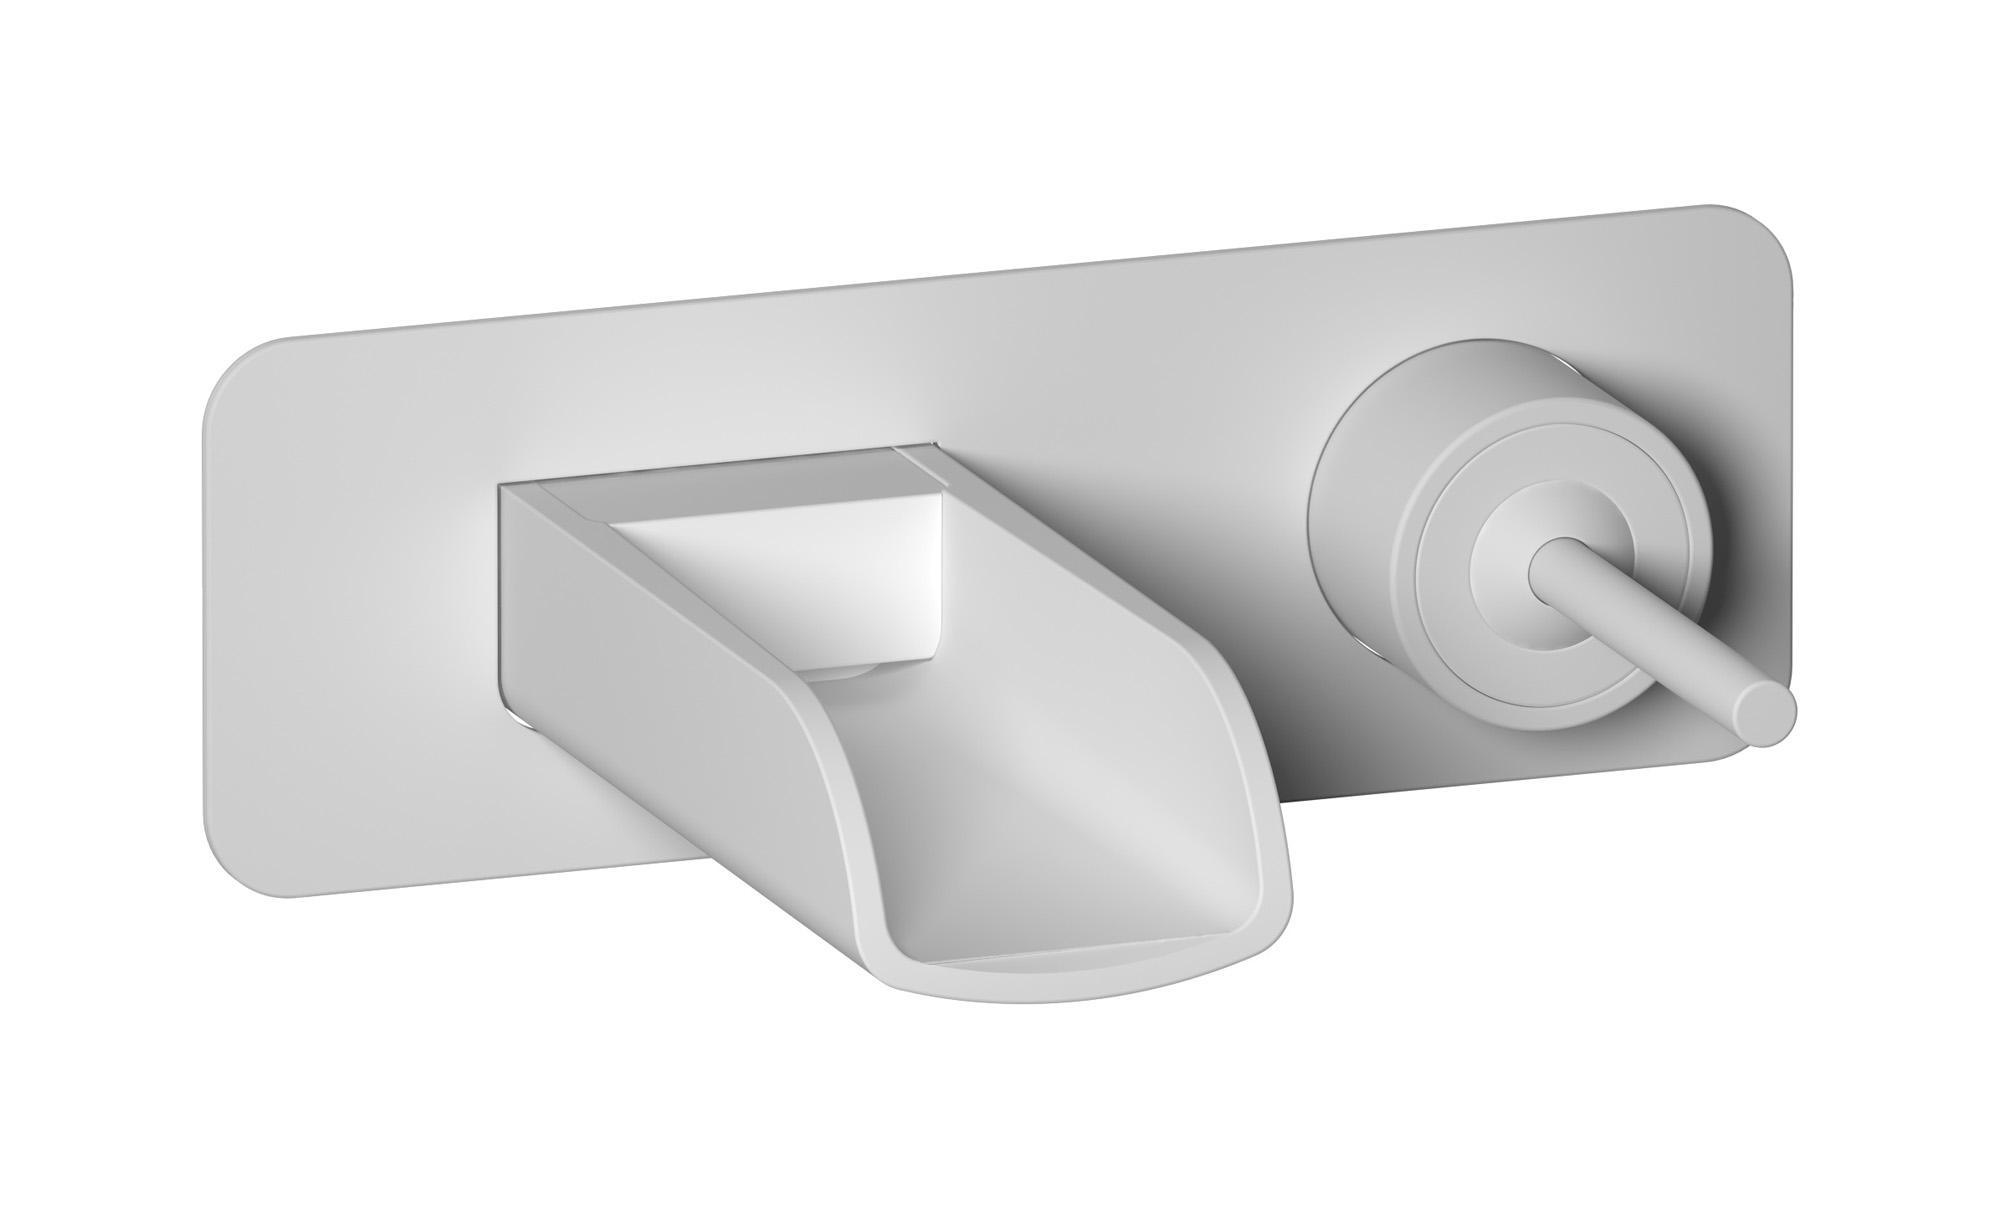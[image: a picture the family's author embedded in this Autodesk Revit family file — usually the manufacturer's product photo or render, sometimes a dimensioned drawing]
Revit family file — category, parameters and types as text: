
# Revit family: LM206
name_source: partatom
category: Apparecchi idraulici
units: mm (PartAtom-declared; Revit-internal decimal feet)

## family parameters
Basato su piano di lavoro = No
Condiviso = No
Mantieni orientamento annotazione = No
Numero OmniClass = 23.45.55.17
Punto di calcolo locali = No
Quota connettore circolare = Usa diametro
Sempre verticale = Sì
Taglio con vuoti quando caricato = No
Tipo di parte = Normale
Titolo OmniClass = Mixing Faucets

## types (9) — shared parameters
Cold water inlet = 10 mm  [stored 0.0328084 ft]
Commenti sul tipo = Washbasin mixer
Connessione CW = No
Connessione HW = No
Connessione di scarico = No
Connessione di ventilazione = No
Descrizione = Wall mounted washbasin mixer complete with drain
Hot water inlet = 10 mm  [stored 0.0328084 ft]
Produttore = IB Rubinetterie S.p.A.
URL = https://www.weareib.it
zero-valued in all types: Prospetto di default

## per-type parameters (varying)
| type | Finishes surface | Immagine tipo | Modello |
| Chrome | IB_Chrome | LM206CC.jpg | LM206CC |
| Brushed nickel | IB_Brushed nickel | LM206SS.jpg | LM206SS |
| Matt white | IB_matt white | LM206BO.jpg | LM206BO |
| Matt black | IB_matt black | LM206NP.jpg | LM206NP |
| Natural brass | IB_Brass | LM206ON.jpg | LM206ON |
| Brushed black chrome | IB_Brushed black chrome | LM206CS.jpg | LM206CS |
| Brushed pale gold | IB_brushed pale gold | LM206IS.jpg | LM206IS |
| Brushed rose gold | IB_Brushed rose gold | LM206SR.jpg | LM206SR |
| Brushed gold | IB_brushed gold | LM206OS.jpg | LM206OS |

note: [stored X ft] marks values corroborated as IEEE doubles in the binary element streams (Revit-internal decimal feet)
